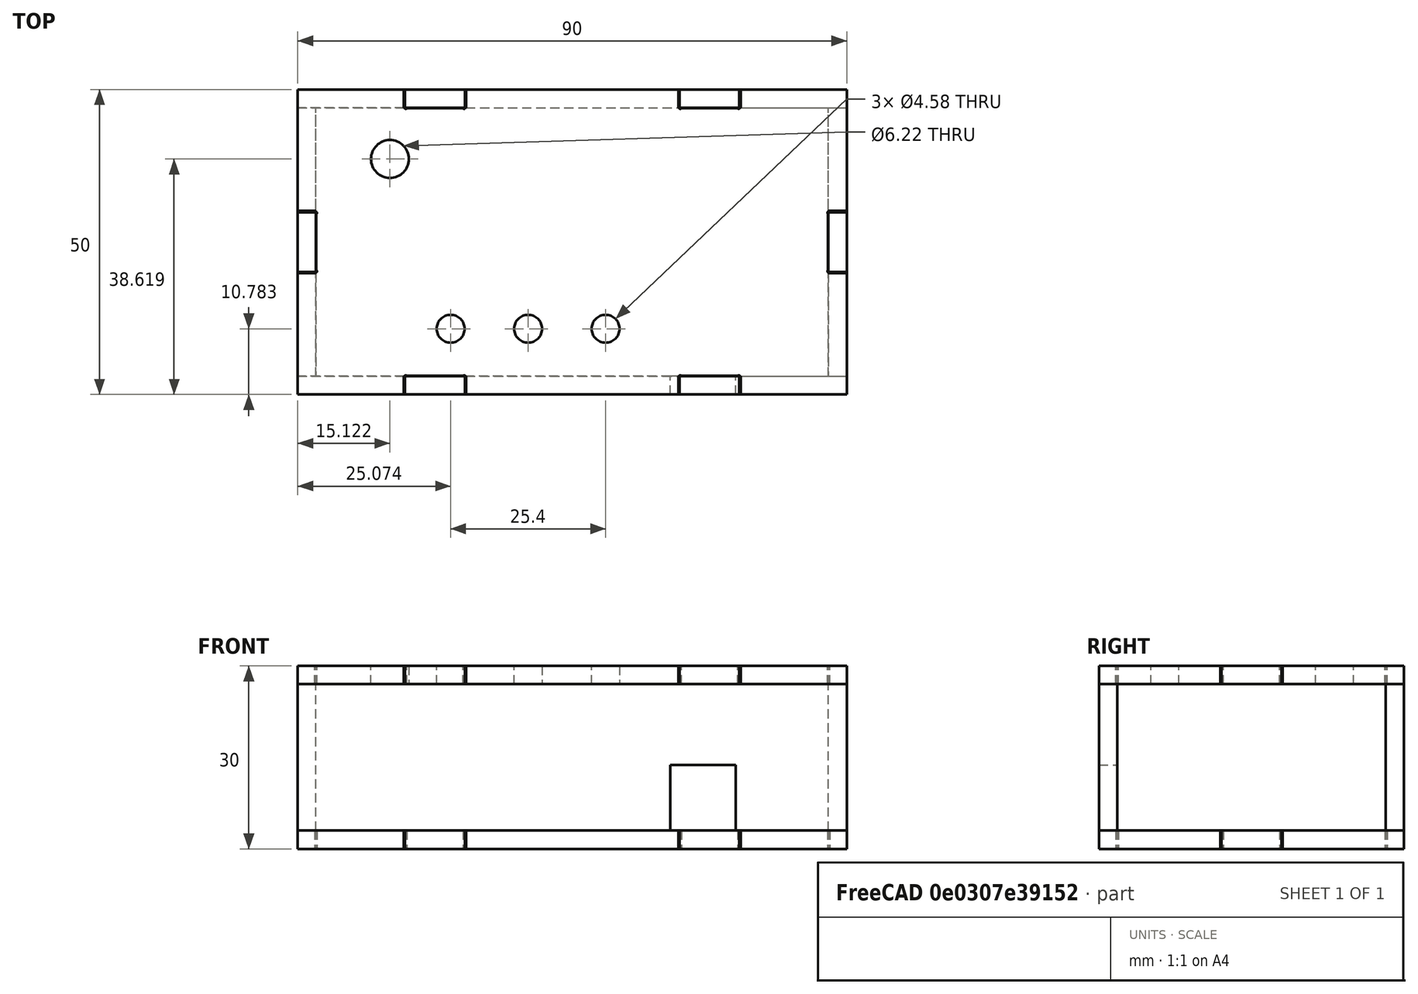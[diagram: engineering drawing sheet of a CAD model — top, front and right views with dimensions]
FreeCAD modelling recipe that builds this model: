
FCSTD DOCUMENT  (FreeCAD 0.18RUnknown)
Label: enclosure
License: All rights reserved
LicenseURL: http://en.wikipedia.org/wiki/All_rights_reserved
objects: Part::Feature×12, Part::FeaturePython×2, Sketcher::SketchObject×2, PartDesign::FeatureBase×2, PartDesign::Pocket×2, PartDesign::Body×2, App::DocumentObjectGroup×1
note: 24 computed .brp shape members not serialized (recipe doc carries the construction recipe); baked Part::Feature solids carry a one-line shape summary decoded from their .brp

FEATURE [Part::Feature] face_panel
  shape: bbox 90 x 3 x 24 mm, 6 faces (baked)
FEATURE [Part::Feature] behind_panel
  Placement = pos=(0,-47,0) rot=(0,0,1;0rad)
  shape: bbox 90 x 3 x 24 mm, 6 faces (baked)
FEATURE [Part::Feature] left_panel
  shape: bbox 3 x 44 x 24 mm, 6 faces (baked)
FEATURE [Part::Feature] right_panel
  Placement = pos=(-87,0,0) rot=(0,0,1;0rad)
  shape: bbox 3 x 44 x 24 mm, 6 faces (baked)
FEATURE [Part::Feature] bottom_panel
  shape: bbox 90 x 50 x 3 mm, 6 faces (baked)
FEATURE [Part::Feature] top_panel
  shape: bbox 90 x 50 x 3 mm, 6 faces (baked)
FEATURE [Part::FeaturePython] Box  # WARN: FeaturePython — macro-defined, semantics opaque (R4)
  parts = -> [face_panel,behind_panel,left_panel,right_panel,bottom_panel,top_panel]
FEATURE [App::DocumentObjectGroup] MultiJoin_origin_parts
  Group = -> [top_panel,behind_panel,right_panel,face_panel,left_panel,bottom_panel]
FEATURE [Part::Feature] top_panel_tab
  shape: bbox 90 x 50 x 3 mm, 48 faces (baked)
FEATURE [Part::Feature] behind_panel_tab
  shape: bbox 90 x 3 x 30 mm, 30 faces (baked)
FEATURE [Part::Feature] right_panel_tab
  shape: bbox 3 x 44 x 30 mm, 18 faces (baked)
FEATURE [Part::Feature] face_panel_tab
  shape: bbox 90 x 3 x 30 mm, 30 faces (baked)
FEATURE [Part::Feature] left_panel_tab
  shape: bbox 3 x 44 x 30 mm, 18 faces (baked)
FEATURE [Part::Feature] bottom_panel_tab
  shape: bbox 90 x 50 x 3 mm, 48 faces (baked)
FEATURE [Part::FeaturePython] MultiJoin  # WARN: FeaturePython — macro-defined, semantics opaque (R4)
  fromParts = -> [MultiJoin_origin_parts,top_panel,behind_panel,right_panel,face_panel,left_panel,bottom_panel]
  generatedParts = -> [top_panel_tab,behind_panel_tab,right_panel_tab,face_panel_tab,left_panel_tab,bottom_panel_tab]
FEATURE [Sketcher::SketchObject] Sketch
  MapMode = 5
  Placement = pos=(0,0,15) rot=(0,0,1;0rad)
  Support = -> [top_panel_tab]
  sketch-geometry (4):
    g0: Circle CenterX=-29.8784 CenterY=13.6189 CenterZ=0 NormalX=0 NormalY=0 NormalZ=1 AngleXU=0 Radius=3.10943
    g1: Circle CenterX=-19.9261 CenterY=-14.2174 CenterZ=0 NormalX=0 NormalY=0 NormalZ=1 AngleXU=0 Radius=2.28993
    g2: Circle CenterX=-7.22611 CenterY=-14.2174 CenterZ=0 NormalX=0 NormalY=0 NormalZ=1 AngleXU=0 Radius=2.28993
    g3: Circle CenterX=5.47389 CenterY=-14.2174 CenterZ=0 NormalX=0 NormalY=0 NormalZ=1 AngleXU=0 Radius=2.28993
  constraints (4):
    c: Horizontal(g1,g2)
    c: Horizontal(g2,g3)
    c: Distance(g1,g2) = 12.7
    c: Distance(g2,g3) = 12.7
FEATURE [PartDesign::FeatureBase] BaseFeature
  BaseFeature = -> behind_panel_tab
FEATURE [Sketcher::SketchObject] Sketch003
  ExternalGeometry = -> [BaseFeature]
  MapMode = 5
  Placement = pos=(0,-25,0) rot=(1,0,0;1.5708rad)
  Support = -> [BaseFeature]
  sketch-geometry (4):
    g0: LineSegment StartX=26.8082 StartY=-12 StartZ=0 EndX=16.085 EndY=-12 EndZ=0
    g1: LineSegment StartX=16.085 StartY=-12 StartZ=0 EndX=16.085 EndY=-1.25242 EndZ=0
    g2: LineSegment StartX=16.085 StartY=-1.25242 StartZ=0 EndX=26.8082 EndY=-1.25242 EndZ=0
    g3: LineSegment StartX=26.8082 StartY=-1.25242 StartZ=0 EndX=26.8082 EndY=-12 EndZ=0
  constraints (9):
    c: Coincident(g0,g1)
    c: Coincident(g1,g2)
    c: Coincident(g2,g3)
    c: Coincident(g3,g0)
    c: Horizontal(g0)
    c: Horizontal(g2)
    c: Vertical(g1)
    c: Vertical(g3)
    c: PointOnObject(g0,g-4)
FEATURE [PartDesign::FeatureBase] BaseFeature001
  BaseFeature = -> top_panel_tab
FEATURE [PartDesign::Pocket] Pocket001
  BaseFeature = -> BaseFeature001
  Length = 5.08
  Length2 = 100.076
  Profile = -> Sketch
  Type = 0
FEATURE [PartDesign::Body] Body001
  BaseFeature = -> top_panel_tab
  Group = -> [BaseFeature001,Sketch,Pocket001]
  Origin = -> Origin001
  Tip = -> Pocket001
FEATURE [PartDesign::Pocket] Pocket
  BaseFeature = -> BaseFeature
  Length = 5.08
  Length2 = 100.076
  Profile = -> Sketch003
  Type = 0
FEATURE [PartDesign::Body] Body
  BaseFeature = -> behind_panel_tab
  Group = -> [BaseFeature,Sketch003,Pocket]
  Origin = -> Origin
  Tip = -> Pocket
